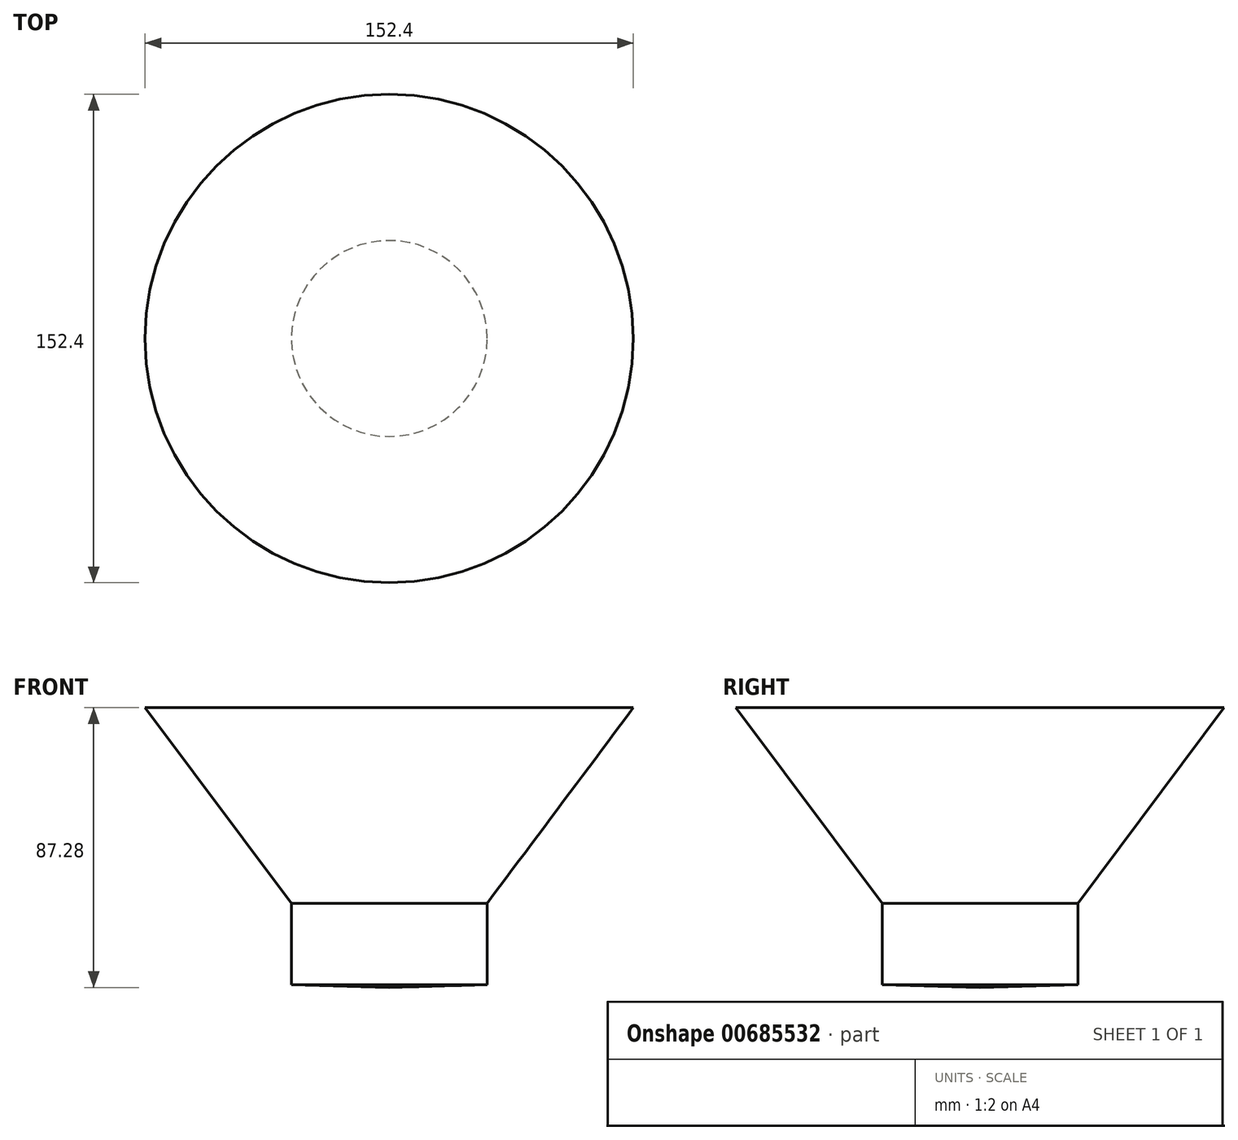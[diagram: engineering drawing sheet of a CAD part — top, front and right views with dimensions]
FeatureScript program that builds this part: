
annotation { "Feature Type Name" : "Feature", "Feature Type Description" : "" }
export const myFeature = defineFeature(function(context is Context, id is Id, definition is map)
    precondition{}
    {
        {
            var Q0;
            Q0=qCreatedBy(makeId("Front.planeOp"),FACE);
            var sketch = newSketch(context, id + "F0", { "sketchPlane" : qUnion([Q0])});
            skLineSegment(sketch, "E0", {"start": v(0, -25.4) * mm, "end": v(0, 0) * mm});
            skLineSegment(sketch, "E1", {"start": v(0, 0) * mm, "end": v(45.64, 61.02) * mm});
            skLineSegment(sketch, "E2", {"start": v(45.64, 61.02) * mm, "end": v(-30.56, 61.02) * mm});
            skLineSegment(sketch, "E3", {"start": v(-30.56, 61.02) * mm, "end": v(-30.56, -26.26) * mm});
            skLineSegment(sketch, "E4", {"start": v(-30.56, -26.26) * mm, "end": v(0, -25.4) * mm});
            skSolve(sketch);
        }
        {
            var Q0;
            Q0=makeQuery(id+"F0.imprint","IMPRINT",FACE,{"disambiguationData":[TD([[makeQuery(id+"F0.imprint","IMPRINT",EDGE,{"derivedFrom":sQuery(id+"F0.wireOp",EDGE,"E0")}),1.0]])]});
            var Q1;
            Q1=sQuery(id+"F0.wireOp",EDGE,"E3");
            revolve(context, id + "F1", {"entities" : qUnion([Q0]), "axis" : qUnion([Q1]), "revolveType" : RevolveType.FULL});
        }
    });
